# Revit family: CMB-WM500F-AA
name_source: partatom
category: 機械設備
revit_build: Autodesk Revit 2016 (Build: 20150220_1215(x64)
units: mm (PartAtom-declared; Revit-internal decimal feet)

## family parameters
OmniClass タイトル = Climate Control (HVAC)
OmniClass 番号 = 23.75.00.00
パーツ タイプ = 標準
ロード時にボイドで切り取り = いいえ
丸型コネクタ寸法 = 半径を使用
作業面に基づく = いいえ
共有 = いいえ
常に垂直 = はい
部屋の計算ポイント = いいえ

## types (6) — shared parameters
Connectable Outdoor/Heat source Unit Capacity = PURY-M400~500YNW-A1(-BS)/PURY-EM400~500YNW-A1(-BS)
Connection pipe of outdoor/heat source unit to M400/M450/M500(High press. Pipe)(O.D.) = 19.05  [stored 0.0625 ft]
Connection pipe of outdoor/heat source unit to M400/M450/M500(Low press. Pipe)(O.D.) = 28.58  [stored 0.0937664 ft]
Cooling Power Input (kW) = 1.5
Depth = 500  [stored 1.64042 ft]
Drain pipe_radius = 13.35  [stored 0.0437992 ft]
External Finish = Galvanized steel plate
Field pipe size[W/WP/WL101-150](Max 20m/40m/60m)(I.D.) = 32.6/32.6/32.6
Field pipe size[W/WP/WL10](Max 20m/40m/60m)(I.D.) = 12/12/12
Field pipe size[W/WP/WL11-15](Max 20m/40m/60m)(I.D.) = 12/12/15.5
Field pipe size[W/WP/WL151-250](Max 20m/40m/60m)(I.D.) = 32.6/32.6/39.6
Field pipe size[W/WP/WL16-25](Max 20m/40m/60m)(I.D.) = 15.5/15.5/15.5
Field pipe size[W/WP/WL251-300](Max 20m/40m/60m)(I.D.) = 32.6/39.6/50.8
Field pipe size[W/WP/WL26-32](Max 20m/40m/60m)(I.D.) = 15.5/19.9/19.9
Field pipe size[W/WP/WL301-750](Max 20m/40m/60m)(I.D.) = 50.8/50.8/50.8
Field pipe size[W/WP/WL33-50](Max 20m/40m/60m)(I.D.) = 19.9/19.9/19.9
Field pipe size[W/WP/WL51-63](Max 20m/40m/60m)(I.D.) = 19.9/25.2/25.2
Field pipe size[W/WP/WL64-80](Max 20m/40m/60m)(I.D.) = 25.2/25.2/25.2
Field pipe size[W/WP/WL81-100](Max 20m/40m/60m)(I.D.) = 25.2/25.2/32.6
Heating Power Input (kW) = 1.5
Height = 1500  [stored 4.92126 ft]
Indoor unit capacity connectable to 1 branch = Model WP/W/WL80 or smaller (Use optional joint pipe combining 2 branches when the total unit capacity exceeds WP/W/WL80.)
Number of branch = 6
Phase = 1
Sound Pressure Level (dB(A)) = 54
Space View = はい
Subcategory = HVAC
URL = http://www.mitsubishielectric.com
Unit Weight (kg) = 209
Water piping diameter To Indoor unit(O.D.) = 22  [stored 0.0721785 ft]
Water piping diameter To Sub HBC(O.D.) = 42  [stored 0.137795 ft]
Width = 800  [stored 2.62467 ft]
モデル = CMB-WM500F-AA
製造元 = Mitsubishi Electric Corporation
説明 = HBC
zero-valued in all types: Equip_No., SerialNumber, TagNumber

## per-type parameters (varying)
| type | Cooling Current (A) | Heating Current (A) | Hertz | Voltage |
| CMB-WM500F-AA_220V_50Hz | 6.82 | 6.82 | 50 Hz | 220 V |
| CMB-WM500F-AA_220V_60Hz | 6.82 | 6.82 | 60 Hz | 220 V |
| CMB-WM500F-AA_230V_50Hz | 6.52 | 6.52 | 50 Hz | 230 V |
| CMB-WM500F-AA_230V_60Hz | 6.52 | 6.52 | 60 Hz | 230 V |
| CMB-WM500F-AA_240V_50Hz | 6.25 | 6.25 | 50 Hz | 240 V |
| CMB-WM500F-AA_240V_60Hz | 6.25 | 6.25 | 60 Hz | 240 V |

note: [stored X ft] marks values corroborated as IEEE doubles in the binary element streams (Revit-internal decimal feet)

## geometry (parser evidence)
native form markers: Blend x40, Sweep x2
no freeform markers — native parametric forms only
